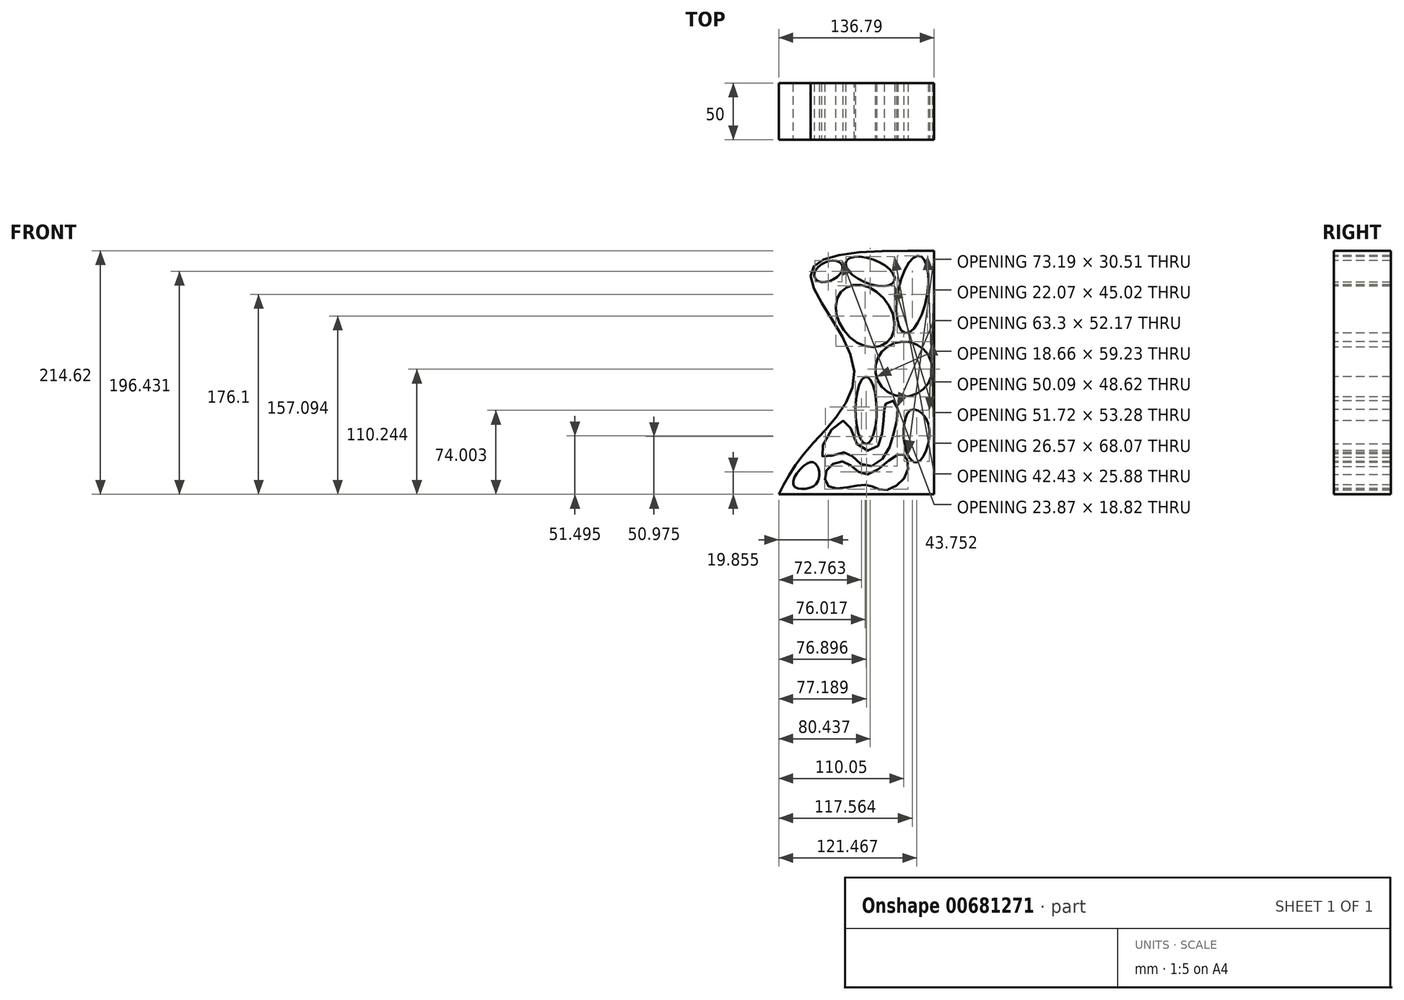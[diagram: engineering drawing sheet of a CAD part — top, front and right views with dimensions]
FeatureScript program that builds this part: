
annotation { "Feature Type Name" : "Feature", "Feature Type Description" : "" }
export const myFeature = defineFeature(function(context is Context, id is Id, definition is map)
    precondition{}
    {
        {
            var Q0;
            Q0=qCreatedBy(makeId("Front.planeOp"),FACE);
            var sketch = newSketch(context, id + "F0", { "sketchPlane" : qUnion([Q0])});
            skLineSegment(sketch, "E0", {"start": v(0, 0) * mm, "end": v(0, 93.17) * mm});
            skLineSegment(sketch, "E1", {"start": v(0, 93.17) * mm, "end": v(0, 214.6) * mm});
            skFitSpline(sketch, "E2", {"points": [v(0, 214.6) * mm, v(-108.5, 195.1) * mm, v(-70.5, 110.24) * mm, v(-112.48, 38.2) * mm, v(-136.8, 0) * mm], "startDerivative": vector(-541.33, 0.47) * mm, "endDerivative": vector(-96.96, -188.74) * mm});
            skLineSegment(sketch, "E3", {"start": v(-136.8, 0) * mm, "end": v(0, 0) * mm});
            skEllipse(sketch, "E4", {"center": v(-93.04, 196.43) * mm, "majorRadius": 13.24 * mm, "minorRadius": 8.4 * mm, "majorAxis": v(-0.9, -0.43)});
            skEllipse(sketch, "E5", {"center": v(-56.35, 196.43) * mm, "majorRadius": 22.82 * mm, "minorRadius": 10.65 * mm, "majorAxis": v(0.93, -0.37)});
            skEllipse(sketch, "E6", {"center": v(-19.23, 176.1) * mm, "majorRadius": 34.6 * mm, "minorRadius": 12.8 * mm, "majorAxis": v(-0.18, -0.98)});
            skEllipse(sketch, "E7", {"center": v(-60.77, 157.1) * mm, "majorRadius": 30.17 * mm, "minorRadius": 22.62 * mm, "majorAxis": v(0.63, -0.78)});
            skEllipse(sketch, "E8", {"center": v(-26.74, 110.24) * mm, "majorRadius": 24.3 * mm, "minorRadius": 25.05 * mm, "majorAxis": v(0, -1)});
            skEllipse(sketch, "E9", {"center": v(-59.9, 74) * mm, "majorRadius": 29.61 * mm, "minorRadius": 9.33 * mm, "majorAxis": v(0, -1)});
            skPoint(sketch, "E10.0.internal.snap0", {"position": v(-50.57, 74) * mm});
            skPoint(sketch, "E10.2.internal.snap0", {"position": v(-50.57, 74) * mm});
            skPoint(sketch, "E10.12.internal.snap0", {"position": v(-50.57, 74) * mm});
            skFitSpline(sketch, "E10", {"points": [v(-43.94, 74) * mm, v(-45.26, 59.42) * mm, v(-50.57, 41.3) * mm, v(-66.04, 41.74) * mm, v(-77.97, 64.72) * mm, v(-96.1, 47.48) * mm, v(-97.42, 32.9) * mm, v(-81.95, 36.88) * mm, v(-72.22, 33.78) * mm, v(-59.85, 24.5) * mm, v(-43.94, 33.34) * mm, v(-35.54, 54.11) * mm, v(-32, 74) * mm, v(-35.98, 82.4) * mm, v(-43.05, 79.3) * mm, v(-43.94, 74) * mm]});
            skFitSpline(sketch, "E11", {"points": [v(-20.95, 74) * mm, v(-24.93, 39.53) * mm, v(-14.32, 28.48) * mm, v(-5.04, 62.07) * mm, v(-20.95, 74) * mm]});
            skFitSpline(sketch, "E12", {"points": [v(-32, 35.1) * mm, v(-59.85, 17.43) * mm, v(-78.41, 28.48) * mm, v(-94.76, 20.96) * mm, v(-92.55, 6.82) * mm, v(-70.9, 7.26) * mm, v(-56.31, 7.7) * mm, v(-43.94, 3.73) * mm, v(-24.93, 16.54) * mm, v(-24.93, 32.9) * mm, v(-32, 35.1) * mm]});
            skFitSpline(sketch, "E13", {"points": [v(-108.9, 28.48) * mm, v(-123.94, 8.59) * mm, v(-106.26, 7.26) * mm, v(-101.4, 20.96) * mm, v(-108.9, 28.48) * mm]});
            skSolve(sketch);
        }
        {
            var Q0;
            Q0=makeQuery(id+"F0.imprint","IMPRINT",FACE,{"disambiguationData":[TD([[makeQuery(id+"F0.imprint","IMPRINT",EDGE,{"derivedFrom":sQuery(id+"F0.wireOp",EDGE,"E0")}),1.0]])]});
            extrude(context, id + "F1", {"entities" : qUnion([Q0]), "endBound" : BoundingType.SYMMETRIC, "oppositeDirection" : true, "depth" : 50 * mm, "offsetDistance" : 25 * mm});
        }
    });
